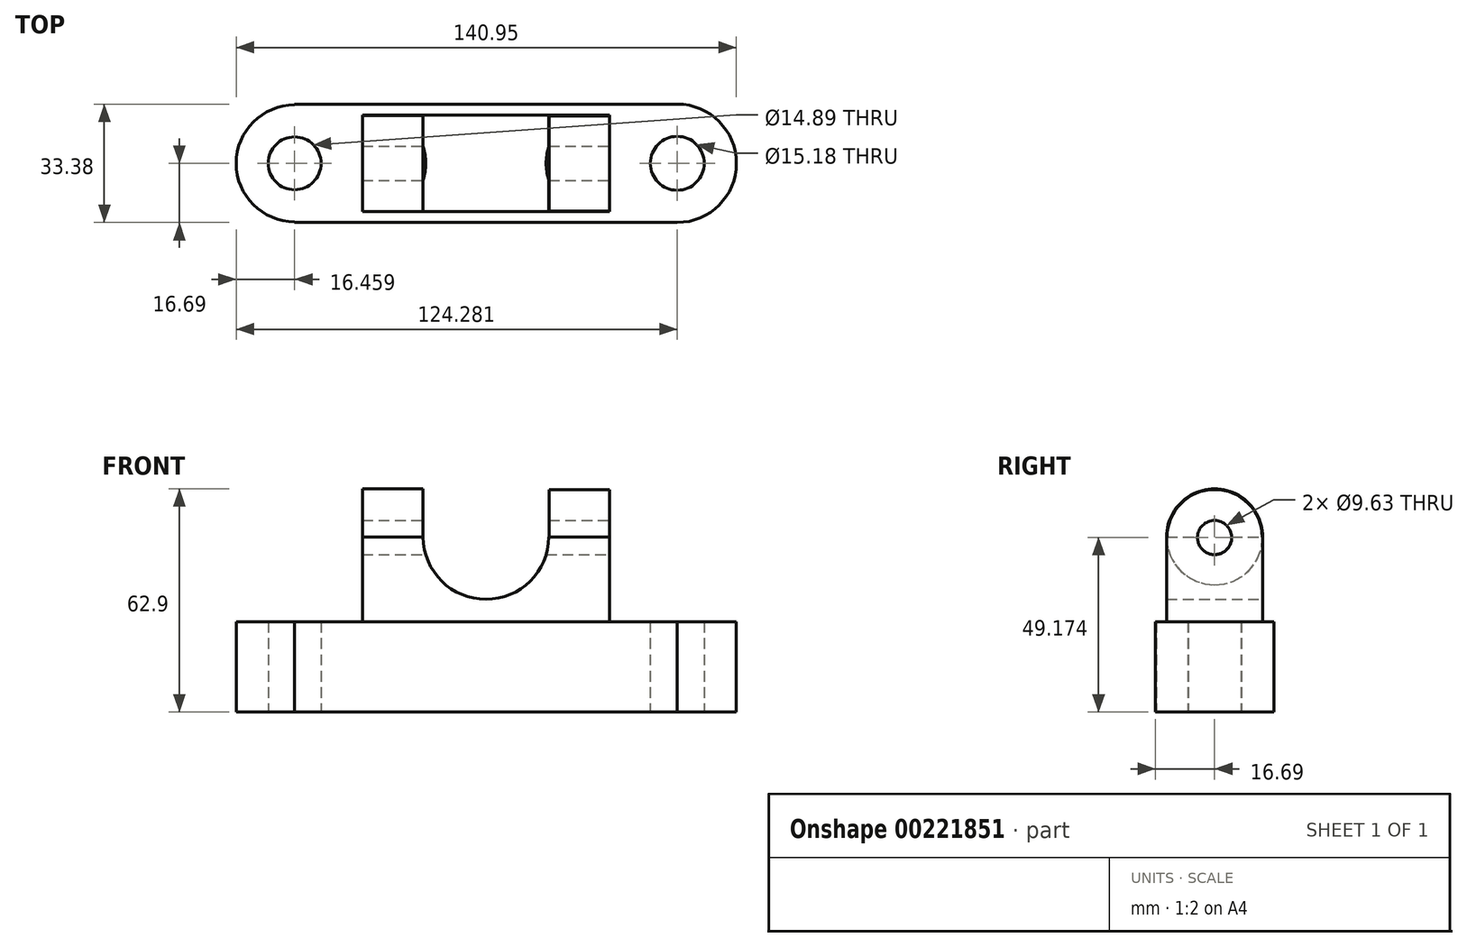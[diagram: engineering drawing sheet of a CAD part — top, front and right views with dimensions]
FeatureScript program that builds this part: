
annotation { "Feature Type Name" : "Feature", "Feature Type Description" : "" }
export const myFeature = defineFeature(function(context is Context, id is Id, definition is map)
    precondition{}
    {
        {
            var Q0;
            Q0=qCreatedBy(makeId("Top.planeOp"),FACE);
            var sketch = newSketch(context, id + "F0", { "sketchPlane" : qUnion([Q0])});
            skLineSegment(sketch, "E0.bottom", {"start": v(-53.91, 16.69) * mm, "end": v(53.91, 16.69) * mm});
            skLineSegment(sketch, "E0.top", {"start": v(-53.91, -16.69) * mm, "end": v(53.91, -16.69) * mm});
            skLineSegment(sketch, "E0.left", {"start": v(-53.91, 16.69) * mm, "end": v(-53.91, 16.45) * mm});
            skLineSegment(sketch, "E0.right", {"start": v(53.91, 16.69) * mm, "end": v(53.91, 16.66) * mm});
            skPoint(sketch, "E0.middle", {"position": v(0, 0) * mm});
            skArc(sketch, "E1", {"start": v(53.91, -16.66) * mm, "mid": v(70.58, 0) * mm, "end": v(53.91, 16.66) * mm});
            skArc(sketch, "E2", {"start": v(-53.91, 16.45) * mm, "mid": v(-70.37, 0) * mm, "end": v(-53.91, -16.45) * mm});
            skLineSegment(sketch, "E3.trimOffspring", {"start": v(53.91, -16.66) * mm, "end": v(53.91, -16.69) * mm});
            skLineSegment(sketch, "E4.trimOffspring", {"start": v(-53.91, -16.45) * mm, "end": v(-53.91, -16.69) * mm});
            skCircle(sketch, "E5", {"center": v(-53.91, 0) * mm, "radius": 7.45 * mm});
            skCircle(sketch, "E6", {"center": v(53.91, 0) * mm, "radius": 7.6 * mm});
            skSolve(sketch);
        }
        {
            var Q0;
            Q0=makeQuery(id+"F0.imprint","IMPRINT",FACE,{"disambiguationData":[TD([[makeQuery(id+"F0.imprint","IMPRINT",EDGE,{"derivedFrom":sQuery(id+"F0.wireOp",EDGE,"E0.bottom")}),-1.0]])]});
            extrude(context, id + "F1", {"entities" : qUnion([Q0]), "depth" : 25.4 * mm});
        }
        {
            var Q0;
            Q0=qCreatedBy(makeId("Top.planeOp"),FACE);
            var sketch = newSketch(context, id + "F2", { "sketchPlane" : qUnion([Q0])});
            skLineSegment(sketch, "E7.bottom", {"start": v(-34.8, 13.55) * mm, "end": v(34.8, 13.55) * mm});
            skLineSegment(sketch, "E7.top", {"start": v(-34.8, -13.55) * mm, "end": v(34.8, -13.55) * mm});
            skLineSegment(sketch, "E7.left", {"start": v(-34.8, 13.55) * mm, "end": v(-34.8, -13.55) * mm});
            skLineSegment(sketch, "E7.right", {"start": v(34.8, 13.55) * mm, "end": v(34.8, -13.55) * mm});
            skPoint(sketch, "E7.middle", {"position": v(0, 0) * mm});
            skSolve(sketch);
        }
        {
            var Q0;
            Q0 = qSketchRegion(id + "F2", true);
            extrude(context, id + "F3", {"entities" : qUnion([Q0]), "operationType" : NewBodyOperationType.ADD, "depth" : 49.28 * mm});
        }
        {
            var Q0;
            Q0=qCreatedBy(makeId("Front.planeOp"),FACE);
            var sketch = newSketch(context, id + "F4", { "sketchPlane" : qUnion([Q0])});
            skCircle(sketch, "E8", {"center": v(0, 49.49) * mm, "radius": 17.73 * mm});
            skSolve(sketch);
        }
        {
            var Q0;
            Q0 = qSketchRegion(id + "F4", true);
            extrude(context, id + "F5", {"entities" : qUnion([Q0]), "operationType" : NewBodyOperationType.REMOVE, "depth" : 17.27 * mm, "hasSecondDirection" : true, "secondDirectionOppositeDirection" : true, "secondDirectionDepth" : 17.27 * mm});
        }
        {
            var Q0;
            Q0=qCreatedBy(makeId("Right.planeOp"),FACE);
            var sketch = newSketch(context, id + "F6", { "sketchPlane" : qUnion([Q0])});
            skCircle(sketch, "E9", {"center": v(0, 49.28) * mm, "radius": 13.4 * mm});
            skSolve(sketch);
        }
        {
            var Q0;
            Q0 = qSketchRegion(id + "F6", true);
            extrude(context, id + "F7", {"entities" : qUnion([Q0]), "operationType" : NewBodyOperationType.ADD, "depth" : 34.8 * mm, "hasSecondDirection" : true, "secondDirectionOppositeDirection" : false, "secondDirectionDepth" : 17.75 * mm});
        }
        {
            var Q0;
            Q0=qCreatedBy(makeId("Right.planeOp"),FACE);
            var sketch = newSketch(context, id + "F8", { "sketchPlane" : qUnion([Q0])});
            skCircle(sketch, "E10", {"center": v(0, 49.38) * mm, "radius": 13.53 * mm});
            skSolve(sketch);
        }
        {
            var Q0;
            Q0 = qSketchRegion(id + "F8", true);
            extrude(context, id + "F9", {"entities" : qUnion([Q0]), "operationType" : NewBodyOperationType.ADD, "oppositeDirection" : true, "depth" : 34.82 * mm, "hasSecondDirection" : true, "secondDirectionOppositeDirection" : true, "secondDirectionDepth" : 17.75 * mm});
        }
        {
            var Q0;
            Q0=qCreatedBy(makeId("Right.planeOp"),FACE);
            var sketch = newSketch(context, id + "F10", { "sketchPlane" : qUnion([Q0])});
            skCircle(sketch, "E11", {"center": v(0, 49.17) * mm, "radius": 4.81 * mm});
            skPoint(sketch, "E12.orphan", {"position": v(0, 63.37) * mm});
            skSolve(sketch);
        }
        {
            var Q0;
            Q0 = qSketchRegion(id + "F10", true);
            extrude(context, id + "F11", {"entities" : qUnion([Q0]), "operationType" : NewBodyOperationType.REMOVE, "oppositeDirection" : true, "depth" : 35.56 * mm, "hasSecondDirection" : true, "secondDirectionOppositeDirection" : false, "secondDirectionDepth" : 35.81 * mm});
        }
    });
